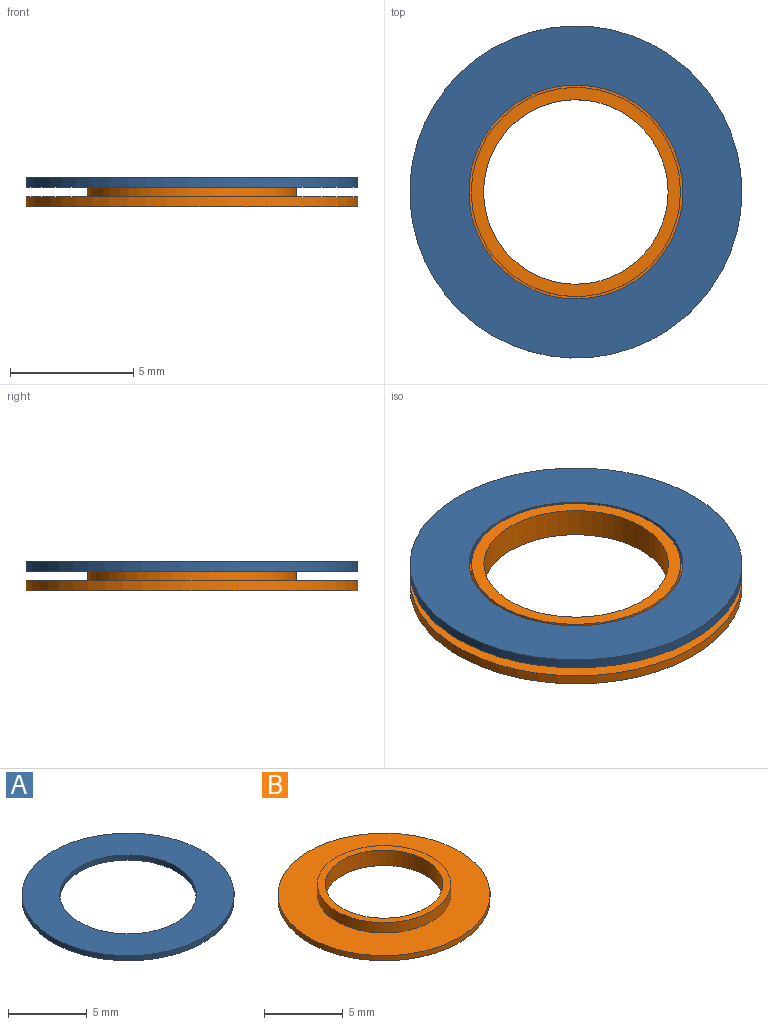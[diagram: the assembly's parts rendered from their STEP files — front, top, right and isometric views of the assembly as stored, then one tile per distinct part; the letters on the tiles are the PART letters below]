
ASSEMBLY  parts=2 mates=1
PART A: 4 faces, bbox 13.5x13.5x0.4 mm
  f0: cylinder r=4.35mm len=8.7mm, axis (0,0,-1), area 10.9mm2, adj f2,f3
  f1: cylinder r=6.75mm len=13.5mm, axis (0,0,-1), area 17mm2, adj f2,f3
  f2: plane 13.5x13.5mm, normal (0,0,1), area 83.7mm2, adj f0,f1
  f3: plane 13.5x13.5mm, normal (0,0,-1), area 83.7mm2, adj f0,f1
PART B: 6 faces, bbox 13.5x13.5x1.2 mm
  f0: cylinder r=3.75mm len=7.5mm, axis (0,0,-1), area 28.3mm2, adj f3,f5
  f1: cylinder r=6.75mm len=13.5mm, axis (0,0,-1), area 17mm2, adj f2,f3
  f2: plane 13.5x13.5mm, normal (0,0,1), area 86.4mm2, adj f1,f4
  f3: plane 13.5x13.5mm, normal (0,0,-1), area 99mm2, adj f0,f1
  f4: cylinder r=4.25mm len=8.5mm, axis (0,0,-1), area 21.4mm2, adj f2,f5
  f5: plane 8.5x8.5mm, normal (0,0,1), area 12.6mm2, adj f0,f4
PLACE A t=(-0.2,0.61,0.89)mm
PLACE B t=(-0.2,0.61,0.09)mm
MATE cylindrical B.f0 <-> A.f0  axis (0,0,1) through (-0.2,0.61,1.29)mm
